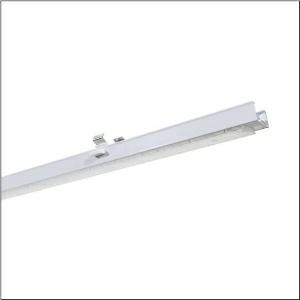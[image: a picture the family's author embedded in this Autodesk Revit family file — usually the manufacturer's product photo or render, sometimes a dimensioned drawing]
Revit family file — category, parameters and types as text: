
# Revit family: trunking_flex_31_51re12db49b
name_source: partatom
category: Lighting Fixtures
units: mm (PartAtom-declared; Revit-internal decimal feet)

## family parameters
Cut with Voids When Loaded = No
Host = Face
Light Source = No
Part Type = Normal
Room Calculation Point = No
Round Connector Dimension = Use Diameter
Shared = No

## types (1)
- Trunking Flex 31 (1 x LED, 8900 lm, 53 W, 4000K)
    Apparent Load = 53 VA
    CIE Flux Codes = 65 91 98 99 100
    Color Rendering = 80
    Color Temperature = 4000K
    Default Elevation = 1800 mm
    Description = Trunking Flex 31, luminaire insert, of extruded aluminium section, coated, traffic white (RAL 9016), length: 1.472mm, width: 91mm, height: 53mm, LED rated luminous flux: 8.900lm, light colour: 840, control gear: DALI 2, with system connector: socket, mains connection: 220..240V, AC, 50/60Hz, rated input power: 53W, primary light control with lens, of plastic, primary optical cover: cover, of PMMA, light emission: direct distribution, protection rating (complete): IP20, insulation class (complete): insulation class I (protective earthing), certification: CE, UKCA, impact resistance: IK02, permissible ambient temperature for indoor applications: -20..+40°C, packaging unit: 1 piece
    Height = 58 mm
    Lamp = 1 x LED
    Lamp Light Flux = 8900 lm
    Lamp Power = 53 W
    Lamp count = 1
    Length = 1472 mm
    Luminous efficacy = 168 lm/W
    Manufacturer = Siteco
    ModVariant = No
    Model = 51RE12DB49B
    Mounting Place = Ceiling
    Mounting Type = Pendant
    Number of Poles = 1
    OnlyDefault = Yes
    Power Factor = 1
    Product Name = Trunking Flex 31
    Product group = luminaire insert
    ProductGroupID = 902
    Protection Class = Protection class I
    Protection Degree = IP 20
    RLX_Detail_Level = 1
    RLX_Emergency_Light_Flux = 0 lm
    RLX_Emergency_Type = 0
    RLX_Emergency_Type_DB = No
    RlxData = <blob elided: 19513 chars, md5=a9e69e45>
    Socket = socket
    Standby Power = 0 W
    System Light Flux = 8900 lm
    System Power = 53 W
    Type Comments = Product without accessories
    Type Image = l_1266702.jpg
    URL = http://relux.com
    VarID = ---
    Voltage = 0 V
    Weight = 0.00 kg
    Width = 65 mm

## geometry (parser evidence)
native form markers: Blend x4, Sweep x10
no freeform markers — native parametric forms only
